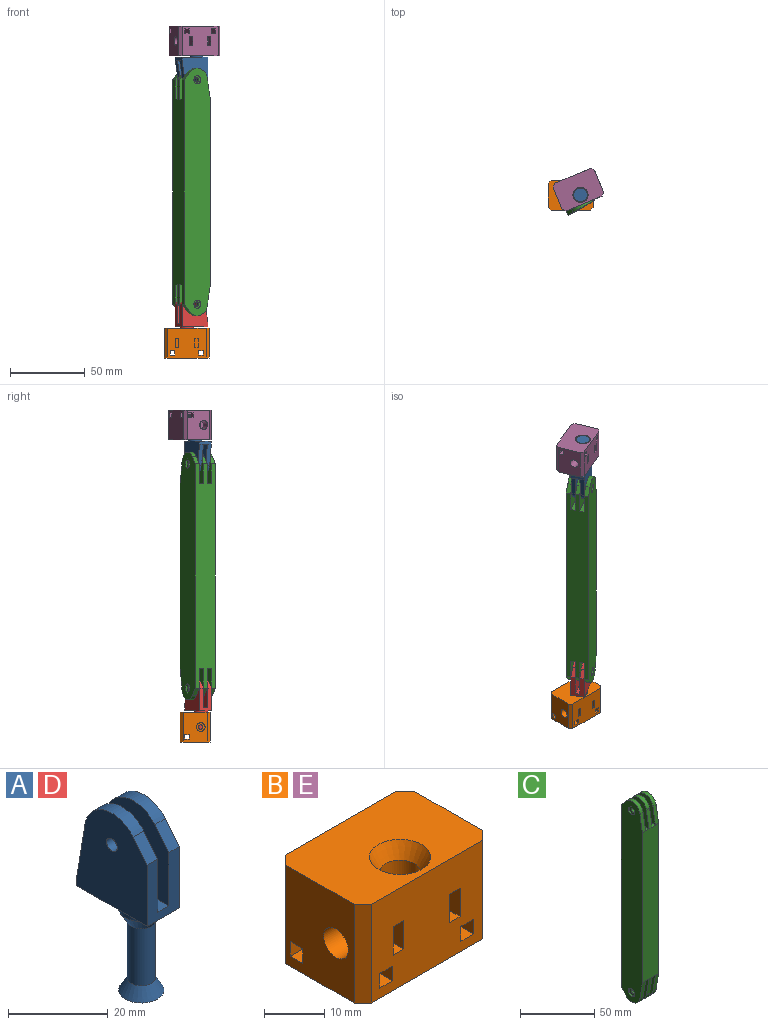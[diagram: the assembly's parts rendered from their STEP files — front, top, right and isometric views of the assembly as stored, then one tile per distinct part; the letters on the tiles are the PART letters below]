
ASSEMBLY  parts=5 mates=4
PART A: 24 faces, bbox 9.1x20x43.8 mm
  f0: cone r=4.55mm half-angle=30deg, axis (0,0,1), area 80.2mm2, adj f1,f4
  f1: cylinder r=2.82mm len=14mm, axis (0,0,1), area 247.9mm2, adj f0,f2
  f2: cone r=2.82mm half-angle=30deg, axis (0,0,-1), area 80.2mm2, adj f1,f3
  f3: plane 9.1x9.1mm, normal (0,0,-1), area 65mm2, adj f2
  f4: cylinder r=4.55mm len=9.1mm, axis (0,0,-1), area 28.6mm2, adj f0,f5,f6
  f5: plane 13.76x9.1mm, normal (0,0,-1), area 92.7mm2, adj f4,f8,f9,f20
  f6: plane 9.1x6.24mm, normal (0,0,-1), area 24.3mm2, adj f4,f7,f8,f9
  f7: plane 15x9.1mm, normal (0,-1,0), area 96.2mm2, adj f6,f8,f9,f10,f11,f12,f13,f14
  f8: plane 22.75x20mm, normal (1,0,0), area 360.6mm2, adj f5,f6,f7,f14,f16,f17,f20,f22
  f9: plane 22.75x20mm, normal (-1,0,0), area 377.3mm2, adj f5,f6,f7,f13,f18,f19,f20,f21
  f10: plane 20x3.1mm, normal (0,0,1), area 62mm2, adj f7,f11,f12,f20
  f11: plane 20.75x20mm, normal (1,0,0), area 337.3mm2, adj f7,f10,f13,f18,f19,f21
  f12: plane 20.75x20mm, normal (-1,0,0), area 337.3mm2, adj f7,f10,f14,f15,f16,f17
  f13: plane 4.9x3.99mm, normal (0,-0.77,0.63), area 19mm2, adj f7,f9,f11,f18
  f14: plane 4.9x3.99mm, normal (0,-0.77,0.63), area 19mm2, adj f7,f8,f12,f16
  f15: cylinder r=1.5mm len=3mm, axis (-1,0,0), area 18.8mm2, adj f12,f23
  f16: cylinder r=7.75mm len=13.65mm, axis (-1,0,0), area 53.3mm2, adj f8,f12,f14,f17
  f17: plane 14.26x3mm, normal (0,0.99,0.16), area 43.4mm2, adj f8,f12,f16,f20
  f18: cylinder r=7.75mm len=13.65mm, axis (-1,0,0), area 53.3mm2, adj f9,f11,f13,f19
  f19: plane 14.26x3mm, normal (0,0.99,0.16), area 43.4mm2, adj f9,f11,f18,f20
  f20: plane 9.1x2mm, normal (0,1,0), area 18.2mm2, adj f5,f8,f9,f10,f17,f19
  f21: cylinder r=1.5mm len=3mm, axis (-1,0,0), area 28.3mm2, adj f9,f11
  f22: cylinder r=2.75mm len=5.5mm, axis (1,0,0), area 17.3mm2, adj f8,f23
  f23: plane 5.5x5.5mm, normal (1,0,0), area 16.7mm2, adj f15,f22
PART B: 45 faces, bbox 30x20x20 mm
  f0: plane 20x16mm, normal (1,0,0), area 285mm2, adj f27,f28,f29,f30,f34,f36,f37,f38
  f1: plane 20x16mm, normal (-1,0,0), area 285mm2, adj f23,f26,f29,f30,f34,f36,f41,f42
  f2: plane 14x3mm, normal (-1,0,0), area 42mm2, adj f6,f34,f36,f40
  f3: plane 14x3mm, normal (1,0,0), area 42mm2, adj f6,f34,f36,f41
  f4: plane 14x3mm, normal (1,0,0), area 42mm2, adj f6,f34,f36,f40
  f5: plane 14x3mm, normal (-1,0,0), area 42mm2, adj f6,f34,f36,f38
  f6: plane 26x20mm, normal (0,-1,0), area 473.3mm2, adj f2,f3,f4,f5,f14,f15,f16,f17
  f7: plane 26x20mm, normal (0,1,0), area 502mm2, adj f29,f30,f31,f32,f33,f34,f35,f36
  f8: cylinder r=1.5mm len=3mm, axis (1,0,0), area 20.5mm2, adj f13,f15
  f9: cylinder r=1.5mm len=3mm, axis (-1,0,0), area 20.5mm2, adj f13,f17
  f10: plane 5.75x2.5mm, normal (0,-1,0), area 14.4mm2, adj f12,f17,f18,f20
  f11: plane 5.75x2.5mm, normal (0,-1,0), area 14.4mm2, adj f14,f15,f16,f21
  f12: plane 5.75x3mm, normal (1,0,0), area 4.3mm2, adj f10,f18,f20,f23
  f13: cylinder r=3.32mm len=14mm, axis (0,0,1), area 277.3mm2, adj f8,f9,f24,f25
  f14: plane 9.24x2.5mm, normal (0,0,-1), area 23.1mm2, adj f6,f11,f15,f21,f22
  f15: plane 9.24x5.75mm, normal (1,0,0), area 46.1mm2, adj f6,f8,f11,f14,f16
  f16: plane 9.24x2.5mm, normal (0,0,1), area 23.1mm2, adj f6,f11,f15,f21,f22
  f17: plane 9.24x5.75mm, normal (-1,0,0), area 46.1mm2, adj f6,f9,f10,f18,f20
  f18: plane 9.24x2.5mm, normal (0,0,-1), area 23.1mm2, adj f6,f10,f12,f17,f19
  f19: plane 6.24x5.75mm, normal (1,0,0), area 22.9mm2, adj f6,f18,f20,f23
  f20: plane 9.24x2.5mm, normal (0,0,1), area 23.1mm2, adj f6,f10,f12,f17,f19
  f21: plane 5.75x3mm, normal (-1,0,0), area 4.3mm2, adj f11,f14,f16,f28
  f22: plane 6.24x5.75mm, normal (-1,0,0), area 22.9mm2, adj f6,f14,f16,f28
  f23: cylinder r=2.88mm len=7.18mm, axis (-1,0,0), area 129.7mm2, adj f1,f12,f19
  f24: cone r=3.32mm half-angle=30deg, axis (0,0,1), area 91.1mm2, adj f13,f30
  f25: cone r=5.05mm half-angle=30deg, axis (0,0,-1), area 91.1mm2, adj f13,f29
  f26: plane 20x2mm, normal (-0.71,-0.71,0), area 56.6mm2, adj f1,f6,f29,f30
  f27: plane 20x2mm, normal (0.71,-0.71,0), area 56.6mm2, adj f0,f6,f29,f30
  f28: cylinder r=2.88mm len=7.18mm, axis (1,0,0), area 129.7mm2, adj f0,f21,f22
  f29: plane 30x20mm, normal (0,0,-1), area 511.9mm2, adj f0,f1,f6,f7,f25,f26,f27,f43
  f30: plane 30x20mm, normal (0,0,1), area 511.9mm2, adj f0,f1,f6,f7,f24,f26,f27,f43
  f31: plane 3x3mm, normal (-1,0,0), area 9mm2, adj f7,f34,f36,f39
  f32: plane 3x3mm, normal (1,0,0), area 9mm2, adj f7,f34,f36,f42
  f33: plane 3x3mm, normal (1,0,0), area 9mm2, adj f7,f34,f36,f39
  f34: plane 30x20mm, normal (0,0,-1), area 192mm2, adj f0,f1,f2,f3,f4,f5,f6,f7
  f35: plane 3x3mm, normal (-1,0,0), area 9mm2, adj f7,f34,f36,f37
  f36: plane 30x20mm, normal (0,0,1), area 192mm2, adj f0,f1,f2,f3,f4,f5,f6,f7
  f37: plane 4x3mm, normal (0,-1,0), area 12mm2, adj f0,f34,f35,f36
  f38: plane 4x3mm, normal (0,1,0), area 12mm2, adj f0,f5,f34,f36
  f39: plane 16x3mm, normal (0,-1,0), area 48mm2, adj f31,f33,f34,f36
  f40: plane 16x3mm, normal (0,1,0), area 48mm2, adj f2,f4,f34,f36
  f41: plane 4x3mm, normal (0,1,0), area 12mm2, adj f1,f3,f34,f36
  f42: plane 4x3mm, normal (0,-1,0), area 12mm2, adj f1,f32,f34,f36
  f43: plane 20x2mm, normal (-0.71,0.71,0), area 56.6mm2, adj f1,f7,f29,f30
  f44: plane 20x2mm, normal (0.71,0.71,0), area 56.6mm2, adj f0,f7,f29,f30
PART C: 58 faces, bbox 15.5x20x165.5 mm
  f0: cylinder r=1.5mm len=3mm, axis (-1,0,0), area 19.8mm2, adj f19,f30
  f1: cylinder r=1.5mm len=3mm, axis (-1,0,0), area 19.8mm2, adj f16,f28
  f2: plane 4.9x3.99mm, normal (0,0.77,0.63), area 19.6mm2, adj f4,f12,f13,f19
  f3: plane 4.9x3.99mm, normal (0,0.77,0.63), area 19.6mm2, adj f5,f12,f15,f20
  f4: cylinder r=7.75mm len=13.65mm, axis (-1,0,0), area 55.1mm2, adj f2,f6,f13,f19
  f5: cylinder r=7.75mm len=13.65mm, axis (-1,0,0), area 55.1mm2, adj f3,f7,f15,f20
  f6: plane 14.26x3.1mm, normal (0,-0.99,0.16), area 44.8mm2, adj f4,f11,f13,f19
  f7: plane 14.26x3.1mm, normal (0,-0.99,0.16), area 44.8mm2, adj f5,f11,f15,f20
  f8: plane 4.9x3.99mm, normal (0,0.77,0.63), area 19.6mm2, adj f9,f12,f14,f16
  f9: cylinder r=7.75mm len=13.65mm, axis (-1,0,0), area 55.1mm2, adj f8,f10,f14,f16
  f10: plane 14.26x3.1mm, normal (0,-0.99,0.16), area 44.8mm2, adj f9,f11,f14,f16
  f11: plane 124x15.5mm, normal (0,-1,0), area 1922mm2, adj f6,f7,f10,f13,f14,f17,f21,f37
  f12: plane 150x15.5mm, normal (0,1,0), area 2163.8mm2, adj f2,f3,f8,f13,f14,f15,f16,f17
  f13: plane 165.5x20mm, normal (1,0,0), area 3121.3mm2, adj f2,f4,f6,f11,f12,f29,f33,f35
  f14: plane 165.5x20mm, normal (-1,0,0), area 3111.5mm2, adj f8,f9,f10,f11,f12,f22,f23,f24
  f15: plane 20.75x20mm, normal (-1,0,0), area 337.3mm2, adj f3,f5,f7,f12,f17,f18
  f16: plane 20.75x20mm, normal (1,0,0), area 337.3mm2, adj f1,f8,f9,f10,f12,f17
  f17: plane 20x3.1mm, normal (0,0,1), area 62mm2, adj f11,f12,f15,f16
  f18: cylinder r=1.5mm len=3.1mm, axis (-1,0,0), area 29.2mm2, adj f15,f20
  f19: plane 20.75x20mm, normal (-1,0,0), area 337.3mm2, adj f0,f2,f4,f6,f12,f21
  f20: plane 20.75x20mm, normal (1,0,0), area 337.3mm2, adj f3,f5,f7,f12,f18,f21
  f21: plane 20x3.1mm, normal (0,0,1), area 62mm2, adj f11,f12,f19,f20
  f22: plane 2.88x1.66mm, normal (0,0.5,-0.87), area 3.3mm2, adj f14,f23,f27,f28
  f23: plane 2.88x1.66mm, normal (0,-0.5,-0.87), area 3.3mm2, adj f14,f22,f24,f28
  f24: plane 3.32x1mm, normal (0,-1,0), area 3.3mm2, adj f14,f23,f25,f28
  f25: plane 2.88x1.66mm, normal (0,-0.5,0.87), area 3.3mm2, adj f14,f24,f26,f28
  f26: plane 2.88x1.66mm, normal (0,0.5,0.87), area 3.3mm2, adj f14,f25,f27,f28
  f27: plane 3.32x1mm, normal (0,1,0), area 3.3mm2, adj f14,f22,f26,f28
  f28: plane 6.64x5.75mm, normal (-1,0,0), area 21.6mm2, adj f1,f22,f23,f24,f25,f26,f27
  f29: cylinder r=2.75mm len=5.5mm, axis (1,0,0), area 17.3mm2, adj f13,f30
  f30: plane 5.5x5.5mm, normal (1,0,0), area 16.7mm2, adj f0,f29
  f31: cylinder r=1.5mm len=3mm, axis (-1,0,0), area 19.8mm2, adj f46,f57
  f32: cylinder r=1.5mm len=3mm, axis (-1,0,0), area 19.8mm2, adj f43,f55
  f33: plane 4.9x3.99mm, normal (0,0.77,-0.63), area 19.6mm2, adj f12,f13,f35,f46
  f34: plane 4.9x3.99mm, normal (0,0.77,-0.63), area 19.6mm2, adj f12,f36,f42,f47
  f35: cylinder r=7.75mm len=13.65mm, axis (-1,0,0), area 55.1mm2, adj f13,f33,f37,f46
  f36: cylinder r=7.75mm len=13.65mm, axis (-1,0,0), area 55.1mm2, adj f34,f38,f42,f47
  f37: plane 14.26x3.1mm, normal (0,-0.99,-0.16), area 44.8mm2, adj f11,f13,f35,f46
  f38: plane 14.26x3.1mm, normal (0,-0.99,-0.16), area 44.8mm2, adj f11,f36,f42,f47
  f39: plane 4.9x3.99mm, normal (0,0.77,-0.63), area 19.6mm2, adj f12,f14,f40,f43
  f40: cylinder r=7.75mm len=13.65mm, axis (-1,0,0), area 55.1mm2, adj f14,f39,f41,f43
  f41: plane 14.26x3.1mm, normal (0,-0.99,-0.16), area 44.8mm2, adj f11,f14,f40,f43
  f42: plane 20.75x20mm, normal (-1,0,0), area 337.3mm2, adj f12,f34,f36,f38,f44,f45
  f43: plane 20.75x20mm, normal (1,0,0), area 337.3mm2, adj f12,f32,f39,f40,f41,f44
  f44: plane 20x3.1mm, normal (0,0,-1), area 62mm2, adj f11,f12,f42,f43
  f45: cylinder r=1.5mm len=3.1mm, axis (-1,0,0), area 29.2mm2, adj f42,f47
  f46: plane 20.75x20mm, normal (-1,0,0), area 337.3mm2, adj f12,f31,f33,f35,f37,f48
  f47: plane 20.75x20mm, normal (1,0,0), area 337.3mm2, adj f12,f34,f36,f38,f45,f48
  f48: plane 20x3.1mm, normal (0,0,-1), area 62mm2, adj f11,f12,f46,f47
  f49: plane 2.88x1.66mm, normal (0,0.5,0.87), area 3.3mm2, adj f14,f50,f54,f55
  f50: plane 2.88x1.66mm, normal (0,-0.5,0.87), area 3.3mm2, adj f14,f49,f51,f55
  f51: plane 3.32x1mm, normal (0,-1,0), area 3.3mm2, adj f14,f50,f52,f55
  f52: plane 2.88x1.66mm, normal (0,-0.5,-0.87), area 3.3mm2, adj f14,f51,f53,f55
  f53: plane 2.88x1.66mm, normal (0,0.5,-0.87), area 3.3mm2, adj f14,f52,f54,f55
  f54: plane 3.32x1mm, normal (0,1,0), area 3.3mm2, adj f14,f49,f53,f55
  f55: plane 6.64x5.75mm, normal (-1,0,0), area 21.6mm2, adj f32,f49,f50,f51,f52,f53,f54
  f56: cylinder r=2.75mm len=5.5mm, axis (1,0,0), area 17.3mm2, adj f13,f57
  f57: plane 5.5x5.5mm, normal (1,0,0), area 16.7mm2, adj f31,f56
PART D: same geometry as A
PART E: same geometry as B
PLACE A rot(axis=(-0.87,0.5,0),180deg) t=(9.75,45.86,321.96)mm
PLACE B t=(8.66,51.49,99.96)mm fixed
PLACE C rot(axis=(0.87,-0.5,0),180deg) t=(11.87,47.19,270.96)mm
PLACE D rot(axis=(0,0,-1),60.2deg) t=(14.09,48.34,99.96)mm
PLACE E rot(axis=(0.2,-0.98,0),180deg) t=(12.79,54.75,321.96)mm
MATE revolute D.f4 <-> B.f25  axis (0,0,-1) through (8.66,45.23,99.96)mm
MATE revolute D.f15 <-> C.f0  axis (0.5,-0.87,0) through (14.18,43.15,135.96)mm
MATE revolute A.f4 <-> E.f25  axis (0,0,1) through (15.18,48.97,321.96)mm
MATE revolute A.f15 <-> C.f56  axis (0.5,-0.87,0) through (14.18,43.15,285.96)mm
